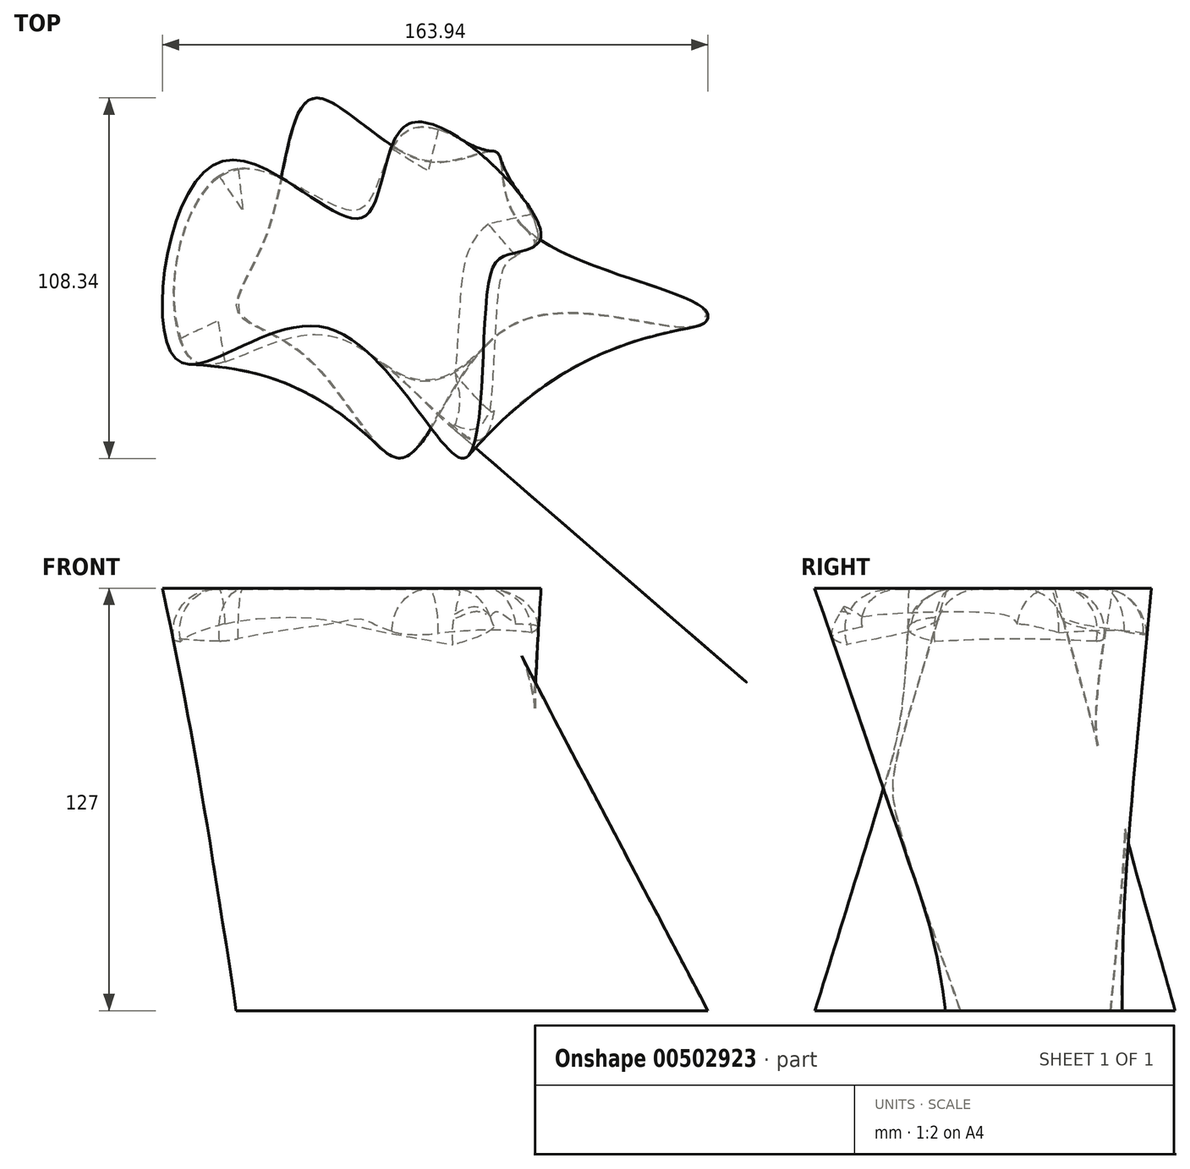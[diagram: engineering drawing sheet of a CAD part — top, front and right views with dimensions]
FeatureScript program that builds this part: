
annotation { "Feature Type Name" : "Feature", "Feature Type Description" : "" }
export const myFeature = defineFeature(function(context is Context, id is Id, definition is map)
    precondition{}
    {
        {
            var Q0;
            Q0=qCreatedBy(makeId("Top.planeOp"),FACE);
            var sketch = newSketch(context, id + "F0", { "sketchPlane" : qUnion([Q0])});
            skFitSpline(sketch, "E0", {"points": [v(9.57, 33.06) * mm, v(-11.75, 30.54) * mm, v(-45.53, 49.3) * mm, v(-59.04, 10.27) * mm, v(-68.4, -14.67) * mm, v(-47.4, -28.76) * mm, v(-18.88, -58.79) * mm, v(14.15, -19) * mm, v(69.33, -19.38) * mm, v(72.33, -14.5) * mm, v(16.78, 11.78) * mm, v(9.57, 33.06) * mm]});
            skSolve(sketch);
        }
        {
            var Q0;
            Q0=qCreatedBy(makeId("Top.planeOp"),FACE);
            cPlane(context, id + "F1", {"entities" : qUnion([Q0]), "cplaneType" : CPlaneType.OFFSET, "offset" : 127 * mm, "width" : 152.4 * mm, "height" : 152.4 * mm});
        }
        {
            var Q0;
            Q0=qCreatedBy(id+"F1.planeOp",FACE);
            var sketch = newSketch(context, id + "F2", { "sketchPlane" : qUnion([Q0])});
            skFitSpline(sketch, "E1", {"points": [v(-30.84, 13.41) * mm, v(-73.76, 30.14) * mm, v(-86.65, -29.2) * mm, v(-41.57, -19.73) * mm, v(0, -58.86) * mm, v(7.35, -4.9) * mm, v(14.35, 2.68) * mm, v(22.87, 8.68) * mm, v(-16.32, 41.82) * mm, v(-30.84, 13.41) * mm]});
            skSolve(sketch);
        }
        {
            var Q0;
            Q0=makeQuery(id+"F0.imprint","IMPRINT",FACE,{"disambiguationData":[TD([[makeQuery(id+"F0.imprint","IMPRINT",EDGE,{"derivedFrom":sQuery(id+"F0.wireOp",EDGE,"E0")}),1.0]])]});
            var Q1;
            Q1=makeQuery(id+"F2.imprint","IMPRINT",FACE,{"disambiguationData":[TD([[makeQuery(id+"F2.imprint","IMPRINT",EDGE,{"derivedFrom":sQuery(id+"F2.wireOp",EDGE,"E1")}),1.0]])]});
            loft(context, id + "F3", {"sheetProfilesArray" : [{ "sheetProfileEntities" : qUnion([Q0]) }, { "sheetProfileEntities" : qUnion([Q1]) }]});
        }
        {
            var Q0;
            Q0=makeQuery(id+"F3.opLoft","CAP_FACE",FACE,{"disambiguationData":[OSD([makeQuery(id+"F0.imprint","IMPRINT",FACE,{"disambiguationData":[TD([[makeQuery(id+"F0.imprint","IMPRINT",EDGE,{"derivedFrom":sQuery(id+"F0.wireOp",EDGE,"E0")}),1.0]])]})])],"isStart":true});
            shell(context, id + "F4", {"entities" : qUnion([Q0]), "thickness" : 0.25 * mm});
        }
        {
            var Q0;
            Q0=makeQuery(id+"F4.opShell","OFFSET_FACE",FACE,{"disambiguationData":[OSD([makeQuery(id+"F2.imprint","IMPRINT",FACE,{"disambiguationData":[TD([[makeQuery(id+"F2.imprint","IMPRINT",EDGE,{"derivedFrom":sQuery(id+"F2.wireOp",EDGE,"E1")}),1.0]])]})])]});
            fillet(context, id + "F5", {"entities" : qUnion([Q0]), "radius" : 12.7 * mm, "tangentPropagation" : true, "allowEdgeOverflow" : false});
        }
    });
